# Revit family: Elkay_Drinking-Water_Bottle-Filling-Stations_EZ_Inwall_St1_Asiapac
name_source: partatom
category: Plumbing Fixtures
units: mm (PartAtom-declared; Revit-internal decimal feet)

## family parameters
Always vertical = Yes
Cut with Voids When Loaded = No
Part Type = Normal
Room Calculation Point = No
Round Connector Dimension = Use Diameter
Shared = No
Work Plane-Based = No

## types (13) — shared parameters
Activation by = Electronic Bottle Filler Sensor
Bottle Filling Station = Yes
Bottle Filling Station Sensor = Yes
Bubbler Style = No Bubbler
Dimensions (L x W x H) = 19 3/4 inch x 3 1/2 inch x 40 13/16 inch
Finish = Stainless Steel
Installation Location = Indoor
Manufacturer = Elkay
Mounting Type = Wall Mount (Inwall Frame/Plate)
Number of Stations = 1
Top Name Plate = Yes
Version = 1.0.0.0

## per-type parameters (varying)
| type | Approx. Shipping Weight | Bottom with Grill | Bottom with out grill | Chilling Capacity | Elkay & Ezh2@ logo | Full Load Amps | H1 | H2 With Grill | H2 With out grill | Inside Bottle Filling Station Elkay Logo | Power | Rated Watts | Sensor Only | Sensor With GreenSpec | Special Features | Top Elkay Logo in Plate |
| LZWSM82K | 80 lbs | Yes | No | 8.0 GPH | Yes | 1 | 518 mm  [stored 1.69948 ft] | 519 mm | 481 mm  [stored 1.57808 ft] | No | 220V/50Hz | 370 | No | Yes | Antimicrobial, Filtered, Green Ticker™, Hands Free, Laminar Flow, Real Drain, Visual Filter Monitor | Yes |
| LZWSM82PK | 80 lbs | Yes | No | 8.0 GPH | Yes | 1 | 557 mm  [stored 1.82743 ft] | 481 mm  [stored 1.57808 ft] | 481 mm  [stored 1.57808 ft] | No | 220V/50Hz | 370 | No | Yes | Antimicrobial, Filtered, Green Ticker™, Hands Free, Laminar Flow, Real Drain, Visual Filter Monitor | Yes |
| LZWSM83K | 80 lbs | Yes | No | 8.0 GPH | Yes | 1 | 518 mm  [stored 1.69948 ft] | 519 mm | 481 mm  [stored 1.57808 ft] | No | 220V/60Hz | 370 | No | Yes | Visual Filter Monitor, Antimicrobial, Filtered, Green Ticker™, Hands Free, Laminar Flow, Real Drain | Yes |
| LZWSM83KSA | 80 lbs | Yes | No | 8.0 GPH | Yes | 1 | 518 mm  [stored 1.69948 ft] | 519 mm | 481 mm  [stored 1.57808 ft] | No | 220V/60Hz | 370 | No | Yes | Hands Free, Visual Filter Monitor, Filtered, Green Ticker™, Laminar Flow, Antimicrobial, Real Drain | Yes |
| LZWSM83PK | 80 lbs | Yes | No | 8.0 GPH | Yes | 1 | 557 mm  [stored 1.82743 ft] | 481 mm  [stored 1.57808 ft] | 481 mm  [stored 1.57808 ft] | No | 220V/60Hz | 370 | No | Yes | Antimicrobial, Filtered, Green Ticker™, Hands Free, Laminar Flow, Real Drain, Visual Filter Monitor | Yes |
| LZWSMDJOK | 33 lbs | No | Yes | Non-refrigerated | No | 1 | 518 mm  [stored 1.69948 ft] | 519 mm | 519 mm | Yes | 220V/50-60Hz | 15 | Yes | No | Antimicrobial, Filtered, Green Ticker™, Hands Free, Laminar Flow, Real Drain, Visual Filter Monitor | Yes |
| LZWSMDJOPK | 33 lbs | Yes | No | Non-refrigerated | Yes | 1 | 557 mm  [stored 1.82743 ft] | 481 mm  [stored 1.57808 ft] | 519 mm | No | 220V/50-60Hz | 15 | No | Yes | Antimicrobial, Filtered, Green Ticker™, Hands Free, Laminar Flow, Real Drain, Visual Filter Monitor | No |
| EZWSM82K | 76 lbs | Yes | No | 8.0 GPH | No | 1 | 518 mm  [stored 1.69948 ft] | 519 mm | 481 mm  [stored 1.57808 ft] | Yes | 220V/50Hz | 370 | No | No | Antimicrobial, Green Ticker™, Hands Free, Laminar Flow, Real Drain | Yes |
| EZWSM82PK | 76 lbs | Yes | No | 8.0 GPH | No | 1 | 557 mm  [stored 1.82743 ft] | 481 mm  [stored 1.57808 ft] | 481 mm  [stored 1.57808 ft] | Yes | 220V/50Hz | 370 | No | No | Antimicrobial, Green Ticker™, Hands Free, Laminar Flow, Real Drain | Yes |
| EZWSM83K | 76 lbs | Yes | No | 8.0 GPH | No | 1 | 518 mm  [stored 1.69948 ft] | 519 mm | 481 mm  [stored 1.57808 ft] | Yes | 220V/60Hz | 370 | No | No | Antimicrobial, Green Ticker™, Hands Free, Laminar Flow, Real Drain | Yes |
| EZWSM83PK | 76 lbs | Yes | No | 8.0 GPH | No | 1 | 557 mm  [stored 1.82743 ft] | 481 mm  [stored 1.57808 ft] | 481 mm  [stored 1.57808 ft] | Yes | 220V/60Hz | 370 | No | No | Antimicrobial, Green Ticker™, Hands Free, Laminar Flow, Real Drain | Yes |
| EZWSMDJOK | 33 lbs | No | Yes | Non-refrigerated | No | 1 | 557 mm  [stored 1.82743 ft] | 519 mm | 481 mm  [stored 1.57808 ft] | Yes | 220V/50-60Hz | 15 | No | No | Antimicrobial, Green Ticker™, Hands Free, Laminar Flow, Real Drain | Yes |
| EZWSMDJOPK | 33 lbs | No | Yes | Non-refrigerated | No | - | 557 mm  [stored 1.82743 ft] | 519 mm | 481 mm  [stored 1.57808 ft] | Yes | 220V/50-60Hz | 15 | No | No | Antimicrobial, Green Ticker™, Hands Free, Laminar Flow, Real Drain | Yes |

note: column(s) folded — value = type name in every type: Model

note: [stored X ft] marks values corroborated as IEEE doubles in the binary element streams (Revit-internal decimal feet)

## geometry (parser evidence)
native form markers: Sweep x38
no freeform markers — native parametric forms only
